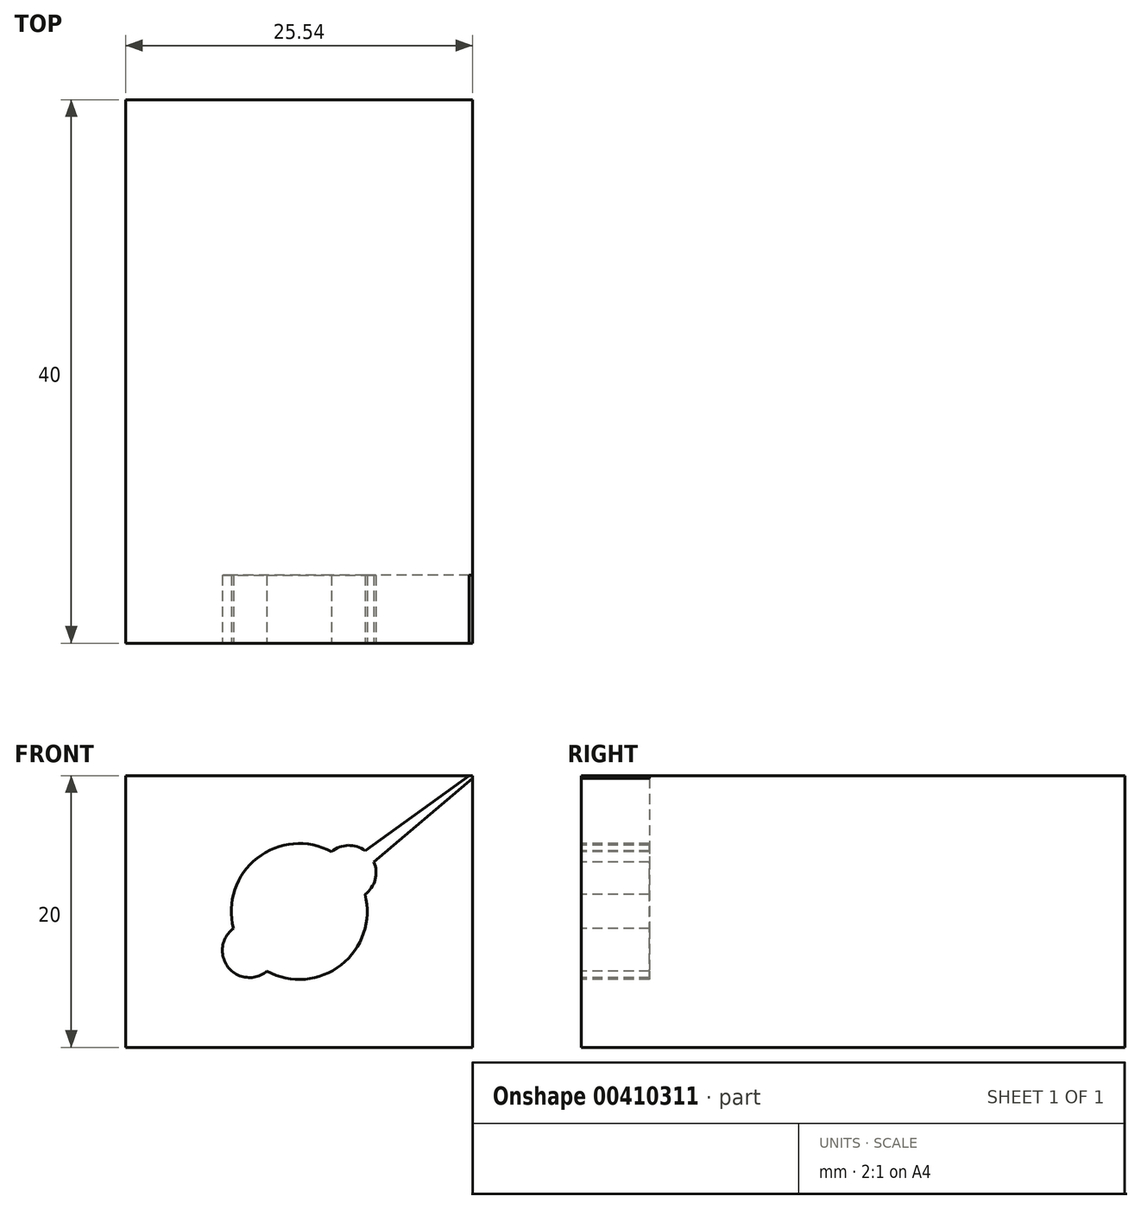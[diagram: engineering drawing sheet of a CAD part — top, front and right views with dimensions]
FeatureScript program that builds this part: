
annotation { "Feature Type Name" : "Feature", "Feature Type Description" : "" }
export const myFeature = defineFeature(function(context is Context, id is Id, definition is map)
    precondition{}
    {
        {
            var Q0;
            Q0=qCreatedBy(makeId("Front.planeOp"),FACE);
            var sketch = newSketch(context, id + "F0", { "sketchPlane" : qUnion([Q0])});
            skLineSegment(sketch, "E0.bottom", {"start": v(12.77, -10) * mm, "end": v(-12.77, -10) * mm});
            skLineSegment(sketch, "E0.top", {"start": v(12.77, 10) * mm, "end": v(-12.77, 10) * mm});
            skLineSegment(sketch, "E0.left", {"start": v(12.77, -10) * mm, "end": v(12.77, 10) * mm});
            skLineSegment(sketch, "E0.right", {"start": v(-12.77, -10) * mm, "end": v(-12.77, 10) * mm});
            skPoint(sketch, "E0.middle", {"position": v(0, 0) * mm});
            skSolve(sketch);
        }
        {
            var Q0;
            Q0=makeQuery(id+"F0.imprint","IMPRINT",FACE,{"disambiguationData":[TD([[makeQuery(id+"F0.imprint","IMPRINT",EDGE,{"derivedFrom":sQuery(id+"F0.wireOp",EDGE,"E0.bottom")}),-1.0]])]});
            extrude(context, id + "F1", {"entities" : qUnion([Q0]), "endBound" : BoundingType.SYMMETRIC, "depth" : 40 * mm});
        }
        {
            var Q0;
            Q0=makeQuery(id+"F1.opExtrude","CAP_FACE",FACE,{"disambiguationData":[OSD([sQuery(id+"F0.wireOp",EDGE,"E0.bottom"),sQuery(id+"F0.wireOp",EDGE,"E0.top"),sQuery(id+"F0.wireOp",EDGE,"E0.left"),sQuery(id+"F0.wireOp",EDGE,"E0.right")])],"isStart":false});
            var sketch = newSketch(context, id + "F2", { "sketchPlane" : qUnion([Q0])});
            skArc(sketch, "E1", {"start": v(2.38, 4.4) * mm, "mid": v(-3.08, 3.94) * mm, "end": v(-4.84, -1.25) * mm});
            skArc(sketch, "E2.trimOffspring", {"start": v(-2.38, -4.4) * mm, "mid": v(3.08, -3.94) * mm, "end": v(4.84, 1.25) * mm});
            skLineSegment(sketch, "E3", {"start": v(14.32, 11.31) * mm, "end": v(4.86, 4.46) * mm});
            skLineSegment(sketch, "E4", {"start": v(14.42, 11.2) * mm, "end": v(5.5, 3.65) * mm});
            skLineSegment(sketch, "E5", {"start": v(0, 0) * mm, "end": v(12.77, 10) * mm, "construction": true});
            skLineSegment(sketch, "E6", {"start": v(14.32, 11.31) * mm, "end": v(14.42, 11.2) * mm});
            skLineSegment(sketch, "E7", {"start": v(0, 10) * mm, "end": v(0, -10) * mm, "construction": true});
            skLineSegment(sketch, "E8.MirrorCS", {"start": v(-14.32, 11.31) * mm, "end": v(-14.42, 11.2) * mm});
            skLineSegment(sketch, "E9", {"start": v(-12.77, 0) * mm, "end": v(12.77, 0) * mm, "construction": true});
            skArc(sketch, "E10", {"start": v(4.84, 1.25) * mm, "mid": v(5.59, 2.34) * mm, "end": v(5.5, 3.65) * mm});
            skArc(sketch, "E11.trimOffspring", {"start": v(4.86, 4.46) * mm, "mid": v(3.6, 4.86) * mm, "end": v(2.38, 4.4) * mm});
            skArc(sketch, "E12", {"start": v(-4.84, -1.25) * mm, "mid": v(-5.23, -4.1) * mm, "end": v(-2.38, -4.4) * mm});
            skLineSegment(sketch, "E13", {"start": v(0, 0) * mm, "end": v(-12.77, -10) * mm, "construction": true});
            skSolve(sketch);
        }
        {
            var Q0;
            Q0 = qSketchRegion(id + "F2", true);
            extrude(context, id + "F3", {"entities" : qUnion([Q0]), "operationType" : NewBodyOperationType.REMOVE, "oppositeDirection" : true, "depth" : 5 * mm});
        }
    });
